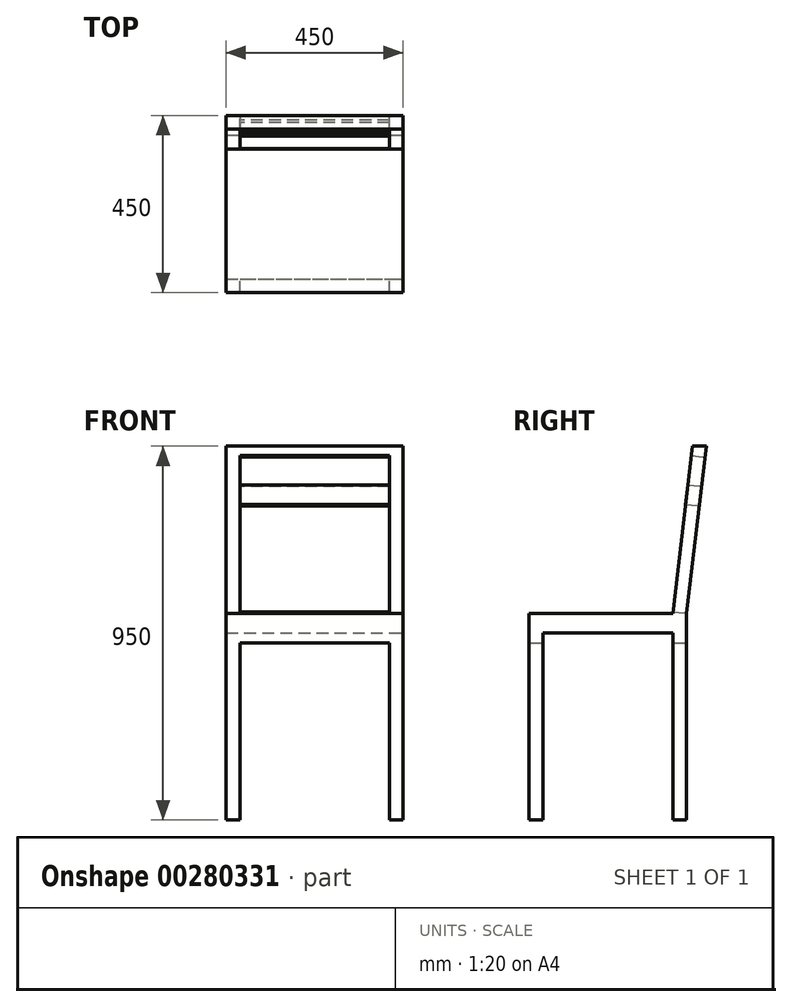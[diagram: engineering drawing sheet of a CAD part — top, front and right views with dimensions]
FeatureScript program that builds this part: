
annotation { "Feature Type Name" : "Feature", "Feature Type Description" : "" }
export const myFeature = defineFeature(function(context is Context, id is Id, definition is map)
    precondition{}
    {
        {
            var Q0;
            Q0=qCreatedBy(makeId("Top.planeOp"),FACE);
            var sketch = newSketch(context, id + "F0", { "sketchPlane" : qUnion([Q0])});
            skLineSegment(sketch, "E0.bottom", {"start": v(225, 225) * mm, "end": v(-225, 225) * mm});
            skLineSegment(sketch, "E0.top", {"start": v(225, -225) * mm, "end": v(-225, -225) * mm});
            skLineSegment(sketch, "E0.left", {"start": v(225, 225) * mm, "end": v(225, -225) * mm});
            skLineSegment(sketch, "E0.right", {"start": v(-225, 225) * mm, "end": v(-225, -225) * mm});
            skPoint(sketch, "E0.middle", {"position": v(0, 0) * mm});
            skSolve(sketch);
        }
        {
            var Q0;
            Q0=qSketchRegion(id+"F0",true);
            extrude(context, id + "F1", {"entities" : qUnion([Q0]), "depth" : 950 * mm});
        }
        {
            var Q0;
            Q0=makeQuery(id+"F1.opExtrude","SWEPT_FACE",FACE,{"disambiguationData":[OSD([sQuery(id+"F0.wireOp",EDGE,"E0.left")])]});
            var sketch = newSketch(context, id + "F2", { "sketchPlane" : qUnion([Q0])});
            skLineSegment(sketch, "E1.bottom", {"start": v(-225, 475) * mm, "end": v(225, 475) * mm});
            skLineSegment(sketch, "E1.top", {"start": v(-225, 525) * mm, "end": v(225, 525) * mm});
            skLineSegment(sketch, "E1.left", {"start": v(-225, 475) * mm, "end": v(-225, 525) * mm});
            skLineSegment(sketch, "E1.right", {"start": v(225, 475) * mm, "end": v(225, 525) * mm});
            skLineSegment(sketch, "E2", {"start": v(175, 525) * mm, "end": v(225, 950) * mm});
            skLineSegment(sketch, "E3", {"start": v(140, 525) * mm, "end": v(190, 950) * mm});
            skLineSegment(sketch, "E4", {"start": v(140, 525) * mm, "end": v(140, 0) * mm});
            skLineSegment(sketch, "E5", {"start": v(175, 525) * mm, "end": v(175, 0) * mm});
            skLineSegment(sketch, "E6", {"start": v(-225, 525) * mm, "end": v(-225, 0) * mm});
            skLineSegment(sketch, "E7", {"start": v(-190, 525) * mm, "end": v(-190, 0) * mm});
            skSolve(sketch);
        }
        {
            var Q0;
            {var subQ0=sQuery(id+"F2.wireOp",EDGE,"E1.right");Q0=makeQuery(id+"F2.imprint","IMPRINT",FACE,{"disambiguationData":[TD([[makeQuery(id+"F2.imprint","IMPRINT",EDGE,{"derivedFrom":subQ0}),-1.0]])]});}
            var Q1;
            {var subQ6=sQuery(id+"F2.wireOp",EDGE,"E3");Q1=makeQuery(id+"F2.imprint","IMPRINT",FACE,{"disambiguationData":[TD([[makeQuery(id+"F2.imprint","IMPRINT",EDGE,{"derivedFrom":subQ6}),1.0]])]});}
            var Q2;
            {var subQ0=sQuery(id+"F2.wireOp",EDGE,"E7");var subQ1=sQuery(id+"F2.wireOp",EDGE,"E1.bottom");var subQ2=makeQuery(id+"F2.imprint","INTERSECT",VERTEX,{"derivedFrom":[subQ1,subQ0]});Q2=makeQuery(id+"F2.imprint","IMPRINT",FACE,{"disambiguationData":[TD([[makeQuery(id+"F2.imprint","IMPRINT",EDGE,{"disambiguationData":[TD([[subQ2,-1.0]])],"derivedFrom":subQ1}),-1.0]])]});}
            var Q3;
            {var subQ1=sQuery(id+"F0.wireOp",EDGE,"E0.left");var subQ4=sQuery(id+"F2.wireOp",EDGE,"E5");var subQ6=makeQuery(id+"F1.opExtrude","CAP_EDGE",EDGE,{"disambiguationData":[OSD([subQ1])],"isStart":true});var subQ7=makeQuery(id+"F2.imprint","INTERSECT",VERTEX,{"derivedFrom":[subQ6,subQ4]});Q3=makeQuery(id+"F2.imprint","IMPRINT",FACE,{"disambiguationData":[TD([[makeQuery(id+"F2.imprint","IMPRINT",EDGE,{"disambiguationData":[TD([[subQ7,1.0]])],"derivedFrom":subQ4}),1.0]])]});}
            var Q4;
            {var subQ4=sQuery(id+"F2.wireOp",EDGE,"E2");Q4=makeQuery(id+"F2.imprint","IMPRINT",FACE,{"disambiguationData":[TD([[makeQuery(id+"F2.imprint","IMPRINT",EDGE,{"derivedFrom":subQ4}),-1.0]])]});}
            extrude(context, id + "F3", {"entities" : qUnion([Q0, Q1, Q2, Q3, Q4]), "operationType" : NewBodyOperationType.REMOVE, "endBound" : BoundingType.THROUGH_ALL, "oppositeDirection" : true, "depth" : 25 * mm});
        }
        {
            var Q0;
            Q0=makeQuery(id+"F3.boolean.opBoolean","COPY",FACE,{"derivedFrom":makeQuery(id+"F3.opExtrude","SWEPT_FACE",FACE,{"disambiguationData":[OSD([sQuery(id+"F2.wireOp",EDGE,"E5")])]})});
            var sketch = newSketch(context, id + "F4", { "sketchPlane" : qUnion([Q0])});
            skLineSegment(sketch, "E8", {"start": v(-190, 0) * mm, "end": v(-190, 450) * mm});
            skLineSegment(sketch, "E9", {"start": v(-190, 450) * mm, "end": v(190, 450) * mm});
            skLineSegment(sketch, "E10", {"start": v(190, 450) * mm, "end": v(190, 0) * mm});
            skSolve(sketch);
        }
        {
            var Q0;
            {var subQ0=sQuery(id+"F4.wireOp",EDGE,"E8");Q0=makeQuery(id+"F4.imprint","IMPRINT",FACE,{"disambiguationData":[TD([[makeQuery(id+"F4.imprint","IMPRINT",EDGE,{"derivedFrom":subQ0}),-1.0]])]});}
            extrude(context, id + "F5", {"entities" : qUnion([Q0]), "operationType" : NewBodyOperationType.REMOVE, "endBound" : BoundingType.THROUGH_ALL, "oppositeDirection" : true, "depth" : 25 * mm});
        }
        {
            var Q0;
            Q0=makeQuery(id+"F3.boolean.opBoolean","COPY",FACE,{"derivedFrom":makeQuery(id+"F3.opExtrude","SWEPT_FACE",FACE,{"disambiguationData":[OSD([sQuery(id+"F2.wireOp",EDGE,"E2")])]})});
            var sketch = newSketch(context, id + "F6", { "sketchPlane" : qUnion([Q0])});
            skLineSegment(sketch, "E11", {"start": v(-190, 541.85) * mm, "end": v(-190, 941.85) * mm});
            skLineSegment(sketch, "E12", {"start": v(-190, 941.85) * mm, "end": v(190, 941.85) * mm});
            skLineSegment(sketch, "E13", {"start": v(190, 941.85) * mm, "end": v(190, 541.85) * mm});
            skSolve(sketch);
        }
        {
            var Q0;
            Q0 = qSketchRegion(id + "F6", true);
            var Q1;
            {var subQ0=sQuery(id+"F6.wireOp",EDGE,"E11");Q1=makeQuery(id+"F6.imprint","IMPRINT",FACE,{"disambiguationData":[TD([[makeQuery(id+"F6.imprint","IMPRINT",EDGE,{"derivedFrom":subQ0}),-1.0]])]});}
            extrude(context, id + "F7", {"entities" : qUnion([Q0, Q1]), "operationType" : NewBodyOperationType.REMOVE, "endBound" : BoundingType.THROUGH_ALL, "oppositeDirection" : true, "depth" : 25 * mm});
        }
        {
            var Q0;
            Q0=makeQuery(id+"F3.boolean.opBoolean","COPY",FACE,{"derivedFrom":makeQuery(id+"F3.opExtrude","SWEPT_FACE",FACE,{"disambiguationData":[OSD([sQuery(id+"F2.wireOp",EDGE,"E2")])]})});
            var sketch = newSketch(context, id + "F8", { "sketchPlane" : qUnion([Q0])});
            skLineSegment(sketch, "E14.bottom", {"start": v(-190, 866.85) * mm, "end": v(190, 866.85) * mm});
            skLineSegment(sketch, "E14.top", {"start": v(-190, 816.85) * mm, "end": v(190, 816.85) * mm});
            skLineSegment(sketch, "E14.left", {"start": v(-190, 866.85) * mm, "end": v(-190, 816.85) * mm});
            skLineSegment(sketch, "E14.right", {"start": v(190, 866.85) * mm, "end": v(190, 816.85) * mm});
            skSolve(sketch);
        }
        {
            var Q0;
            Q0=makeQuery(id+"F8.imprint","IMPRINT",FACE,{"disambiguationData":[TD([[makeQuery(id+"F8.imprint","IMPRINT",EDGE,{"derivedFrom":sQuery(id+"F8.wireOp",EDGE,"E14.bottom")}),-1.0]])]});
            extrude(context, id + "F9", {"entities" : qUnion([Q0]), "oppositeDirection" : true, "depth" : 35 * mm});
        }
        {
            var Q0;
            Q0=makeQuery(id+"F9.opExtrude","CAP_FACE",FACE,{"disambiguationData":[OSD([sQuery(id+"F8.wireOp",EDGE,"E14.bottom"),sQuery(id+"F8.wireOp",EDGE,"E14.top"),sQuery(id+"F8.wireOp",EDGE,"E14.left"),sQuery(id+"F8.wireOp",EDGE,"E14.right")])],"isStart":false});
            extrude(context, id + "F10", {"entities" : qUnion([Q0]), "operationType" : NewBodyOperationType.ADD, "oppositeDirection" : true, "depth" : 25 * mm});
        }
    });
